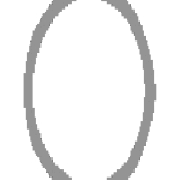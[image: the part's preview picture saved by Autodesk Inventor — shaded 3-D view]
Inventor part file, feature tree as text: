
AUTODESK INVENTOR PART (.ipt)
format: ipt  version: 2021 (Build 250183000, 183)  size: 110,080 bytes
history: native  units: in
note: dims shown in document units (in); Inventor stores cm internally (conversion verified against a paired STEP export)
features: other x4, sketch x3, plane x1
ambient origin geometry x8: Origin, YZ Plane, XZ Plane, XY Plane, X Axis, Y Axis, Z Axis, Center Point
bodies: Solid1 (feature_tree), Body (feature_tree)
feature tree (8):
  other  "Driven Length"
  other  "Frame Generator"
  other  "Start Plane"
  other  "End Plane"
  sketch  "Sketch"  dims[d2=15.2522in d4=-0.0in d5=15.2522in d6=0.12in d7=0.0in d10=90.0deg d9=15.2522in]
  sketch  "Sketch4"  dims[d0=1.0in]
  plane  "Work Plane4"
  sketch  "Sketch5"  dims[d1=0.065in]
